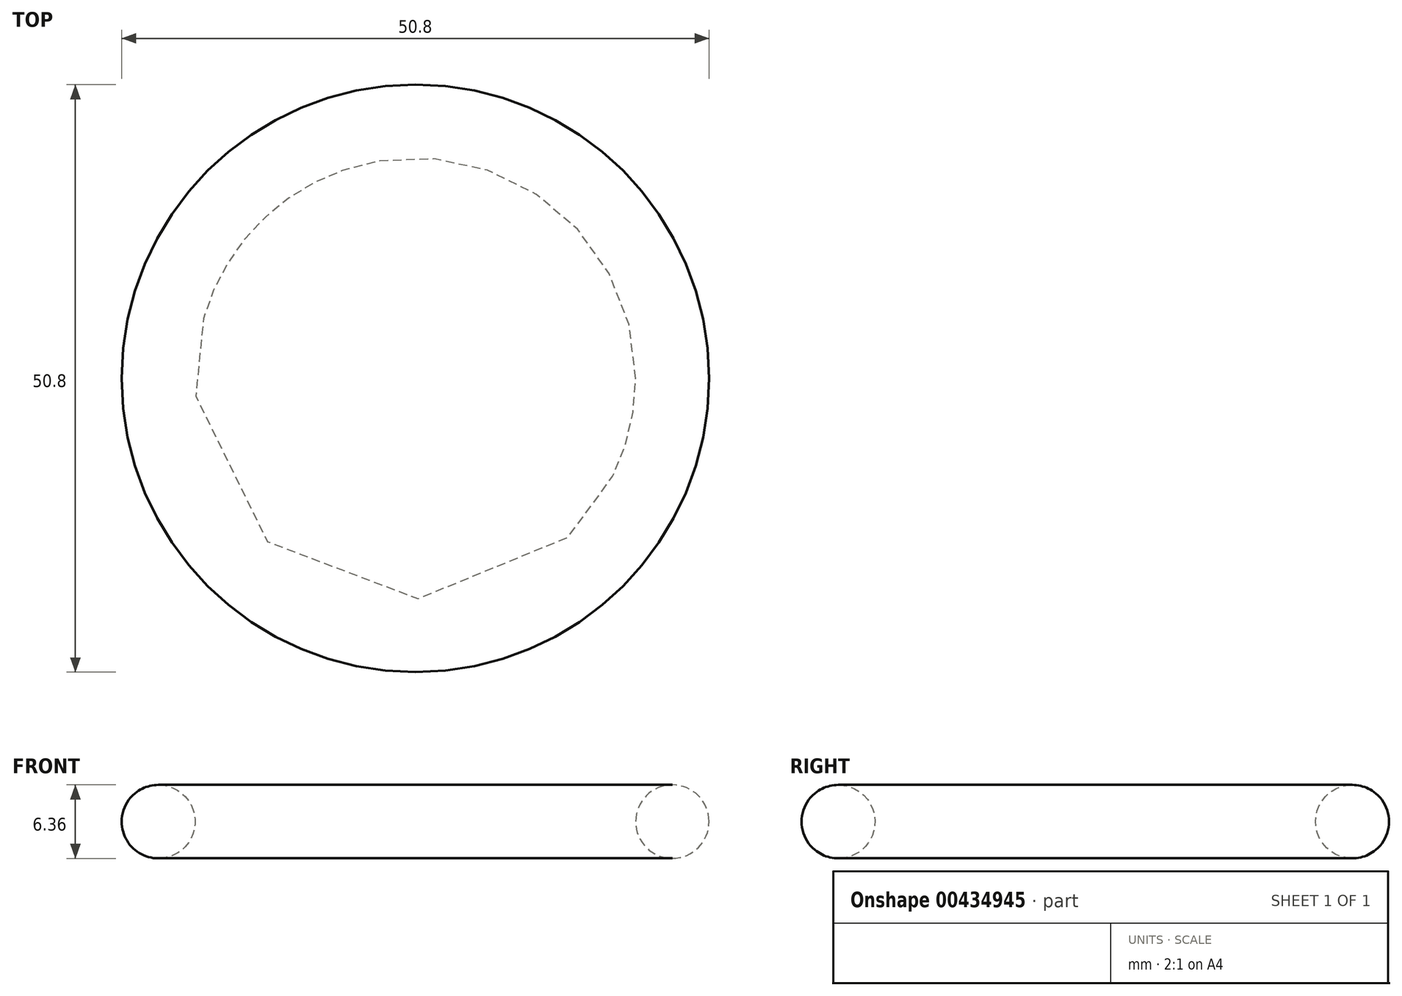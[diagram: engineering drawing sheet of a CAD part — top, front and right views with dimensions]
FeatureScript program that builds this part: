
annotation { "Feature Type Name" : "Feature", "Feature Type Description" : "" }
export const myFeature = defineFeature(function(context is Context, id is Id, definition is map)
    precondition{}
    {
        {
            var Q0;
            Q0=qCreatedBy(makeId("Front.planeOp"),FACE);
            var sketch = newSketch(context, id + "F0", { "sketchPlane" : qUnion([Q0])});
            skCircle(sketch, "E0", {"center": v(-22.22, 0) * mm, "radius": 3.18 * mm});
            skLineSegment(sketch, "E1", {"start": v(0, 19.63) * mm, "end": v(0, -17.84) * mm, "construction": true});
            skSolve(sketch);
        }
        {
            var Q0;
            Q0 = qSketchRegion(id + "F0", true);
            var Q1;
            Q1=sQuery(id+"F0.wireOp",EDGE,"E1");
            revolve(context, id + "F1", {"entities" : qUnion([Q0]), "axis" : qUnion([Q1]), "revolveType" : RevolveType.FULL});
        }
    });
